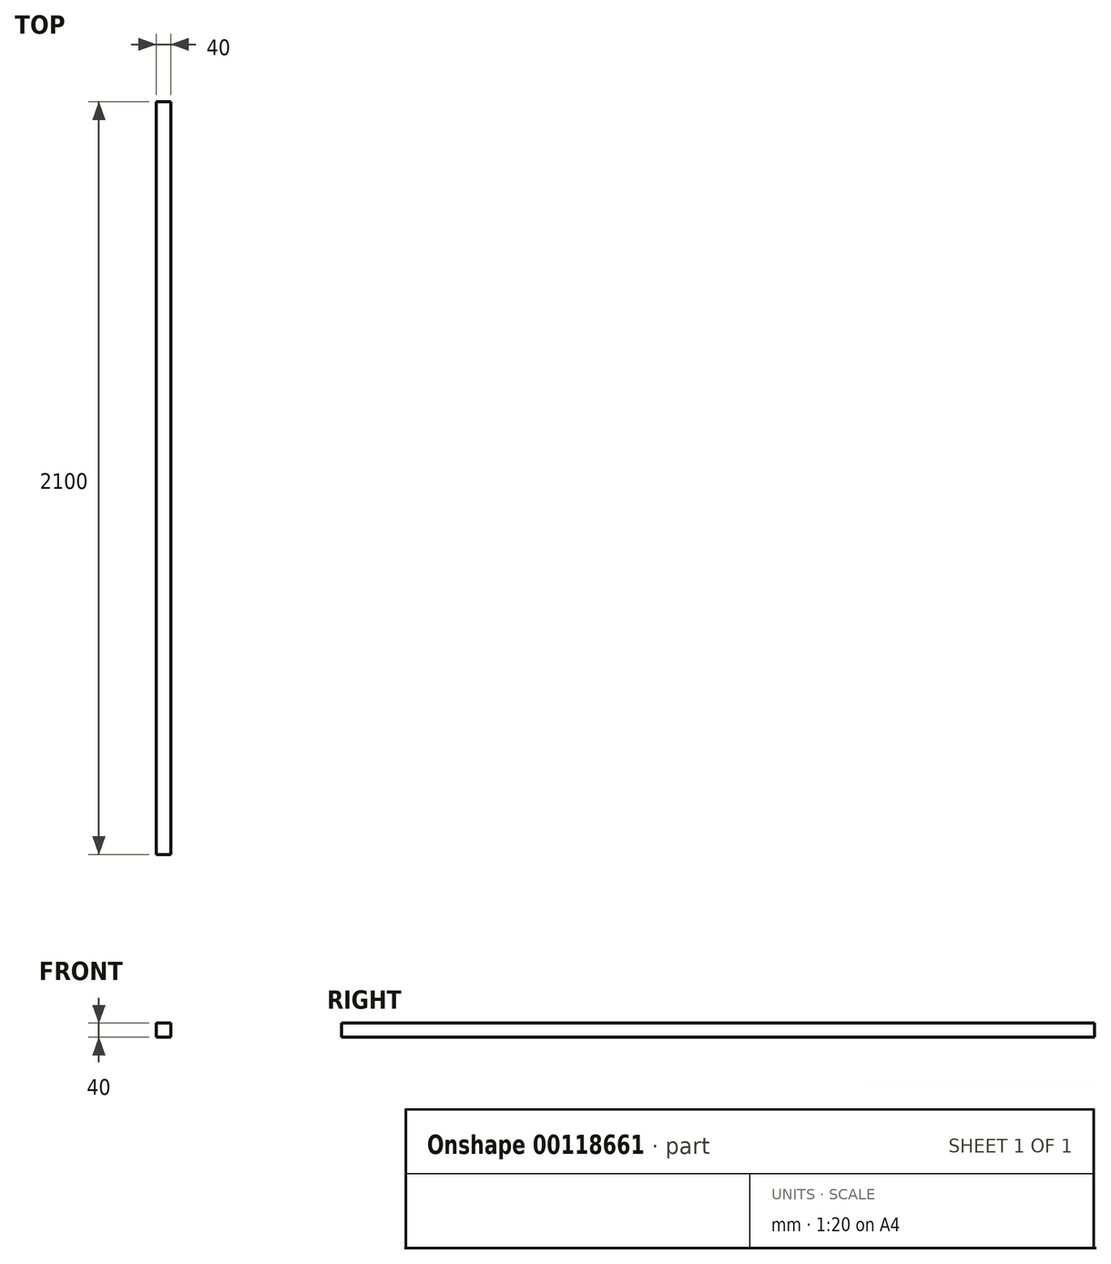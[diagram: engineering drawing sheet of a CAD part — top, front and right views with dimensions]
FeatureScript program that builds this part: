
annotation { "Feature Type Name" : "Feature", "Feature Type Description" : "" }
export const myFeature = defineFeature(function(context is Context, id is Id, definition is map)
    precondition{}
    {
        {
            var Q0;
            Q0=qCreatedBy(makeId("Front.planeOp"),FACE);
            var sketch = newSketch(context, id + "F0", { "sketchPlane" : qUnion([Q0])});
            skLineSegment(sketch, "E0.bottom", {"start": v(0, 0) * mm, "end": v(40, 0) * mm});
            skLineSegment(sketch, "E0.top", {"start": v(0, 40) * mm, "end": v(40, 40) * mm});
            skLineSegment(sketch, "E0.left", {"start": v(0, 0) * mm, "end": v(0, 40) * mm});
            skLineSegment(sketch, "E0.right", {"start": v(40, 0) * mm, "end": v(40, 40) * mm});
            skSolve(sketch);
        }
        {
            var Q0;
            Q0=makeQuery(id+"F0.imprint","IMPRINT",FACE,{"disambiguationData":[TD([[makeQuery(id+"F0.imprint","IMPRINT",EDGE,{"derivedFrom":sQuery(id+"F0.wireOp",EDGE,"E0.bottom")}),1.0]])]});
            extrude(context, id + "F1", {"entities" : qUnion([Q0]), "depth" : 2100 * mm});
        }
    });
